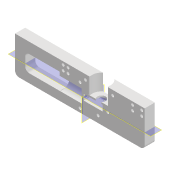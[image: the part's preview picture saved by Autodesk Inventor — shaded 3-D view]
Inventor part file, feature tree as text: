
AUTODESK INVENTOR PART (.ipt)
format: ipt  version: 2022 (Build 260153000, 153)  size: 257,536 bytes
history: native  units: mm
features: reference x15, sketch x11, extrude x10, other x8, plane x6, projected_geometry x4, fillet x3, hole x1
ambient origin geometry x8: Origin, YZ Plane, XZ Plane, XY Plane, X Axis, Y Axis, Z Axis, Center Point
bodies: Solid1 (feature_tree)
feature tree (58):
  extrude  "Extrusion1"  Depth=10.0mm TaperAngle=0.0deg
  fillet  "Fillet1"  Radius=4.0mm
  hole  "Bohrung2"  [1 undecoded]
  extrude  "Extrusion36"  TaperAngle=0.0deg  [1 undecoded]
  extrude  "Extrusion37"  Depth=44.0mm
  plane  "Arbeitsebene10"
  extrude  "Extrusion39"  Depth=4.0mm TaperAngle=0.0deg
  fillet  "Rundung7"  Radius=4.0mm
  sketch  "Skizze43"  dims[d190=0.1mm d191=66.8mm d192=0.0mm]
  plane  "Arbeitsebene11"
  extrude  "Extrusion40"  Depth=0.1mm TaperAngle=0.0deg
  plane  "Arbeitsebene14"
  extrude  "Extrusion41"  Depth=16.0mm TaperAngle=0.0deg
  sketch  "Skizze45"  dims[d197=18.0mm d198=1.0mm d199=10.0mm]
  plane  "Arbeitsebene12"
  extrude  "Extrusion42"  Depth=1.0mm
  fillet  "Rundung8"  Radius=10.0mm
  sketch  "Skizze47"  dims[d204=8.0mm d205=17.0mm d206=0.0mm]
  plane  "Arbeitsebene13"
  extrude  "Extrusion44"  Depth=17.0mm TaperAngle=0.0deg
  sketch  "Skizze48"  dims[d207=0.25mm d208=66.8mm d209=0.0mm]
  plane  "Arbeitsebene15"
  extrude  "Extrusion45"  Depth=66.8mm TaperAngle=0.0deg
  extrude  "Extrusion46"  [1 undecoded]
  sketch  "Sketch1"  dims[d0=127.8mm d2=10.0mm d3=0.0mm d4=4.0mm]
  sketch  "Skizze38"  dims[d169=2.8mm d170=6.0mm d171=4.0mm d172=2.0mm d173=90.0deg d174=8.0mm d175=20.594885mm d176=0.0mm d177=0.0mm]
  projected_geometry  "Projizierte Kontur16"
  sketch  "Skizze39"  dims[d178=63.9mm d179=0.0mm]
  projected_geometry  "Projizierte Kontur17"
  sketch  "Skizze40"  dims[d180=10.0mm d181=0.0mm d185=44.0mm]
  reference  "Referenz22"
  reference  "Referenz23"
  reference  "Referenz24"
  reference  "Referenz25"
  reference  "Referenz26"
  reference  "Referenz27"
  reference  "Referenz28"
  reference  "Referenz29"
  reference  "Referenz30"
  sketch  "Skizze42"  dims[d186=25.0mm d187=66.8mm d188=0.0mm d189=4.0mm]
  projected_geometry  "Projizierte Kontur18"
  reference  "Referenz33"
  sketch  "Skizze44"  dims[d193=10.0mm d194=0.0mm d195=16.0mm d196=0.0mm]
  reference  "Referenz35"
  projected_geometry  "Projizierte Kontur19"
  reference  "Referenz36"
  reference  "Referenz37"
  reference  "Referenz38"
  sketch  "Skizze49"  dims[d210=10.0mm d211=0.0mm]
  reference  "Referenz39"
  other  "<userpath>\Documents\GitHub\Guinardia\INVENTOR\Assembly_HoLiSheet_TwoHalf_v1.iam"
  other  "Assembly_HoLiSheet_TwoHalf_v1.iam"
  other  "10_Wellplate_base_p1_v1:1"
  other  "<userpath>\Documents\GitHub\Guinardia\INVENTOR\Assembly_HoLiSheet_v1.iam"
  other  "Assembly_HoLiSheet_v1.iam"
  other  "00_huawei_p30_Objectivelensassembly:1"
  other  "00_CCTV_lens_M12_25mm_5mp:1"
  other  "20_SMAConnector_fiber:1"
note: 3 required parameter values undecoded (feature->parameter linkage not recoverable at this tier; creation-order binding heuristic only, values carry confidence <= 0.55)
